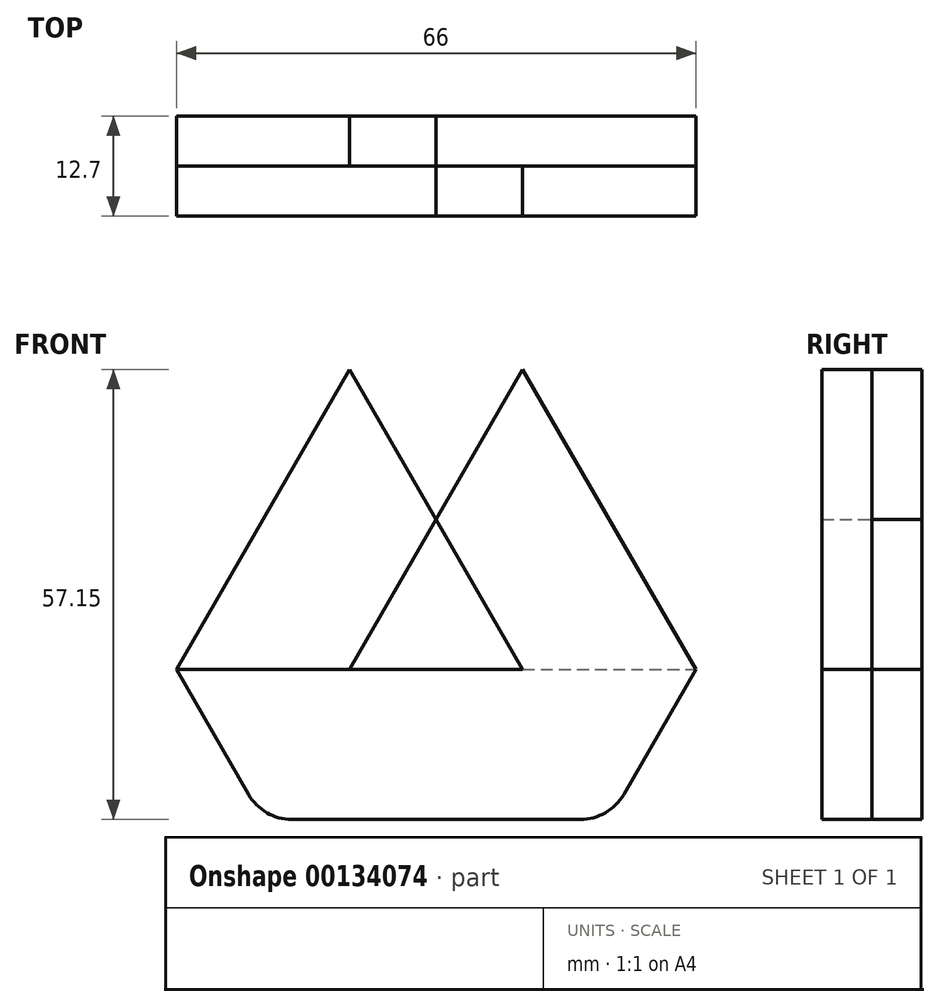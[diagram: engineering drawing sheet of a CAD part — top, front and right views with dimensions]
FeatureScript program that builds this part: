
annotation { "Feature Type Name" : "Feature", "Feature Type Description" : "" }
export const myFeature = defineFeature(function(context is Context, id is Id, definition is map)
    precondition{}
    {
        {
            var Q0;
            Q0=qCreatedBy(makeId("Front.planeOp"),FACE);
            var sketch = newSketch(context, id + "F0", { "sketchPlane" : qUnion([Q0])});
            skLineSegment(sketch, "E0", {"start": v(-11, 57.15) * mm, "end": v(0, 38.1) * mm});
            skLineSegment(sketch, "E1", {"start": v(0, 38.1) * mm, "end": v(11, 57.15) * mm});
            skLineSegment(sketch, "E2", {"start": v(0, 38.1) * mm, "end": v(-11, 19.05) * mm});
            skLineSegment(sketch, "E3", {"start": v(-11, 19.05) * mm, "end": v(11, 19.05) * mm});
            skLineSegment(sketch, "E4", {"start": v(11, 19.05) * mm, "end": v(0, 38.1) * mm});
            skLineSegment(sketch, "E5", {"start": v(11, 57.15) * mm, "end": v(33, 19.05) * mm});
            skLineSegment(sketch, "E6", {"start": v(33, 19.05) * mm, "end": v(23.83, 3.17) * mm});
            skLineSegment(sketch, "E7", {"start": v(18.33, 0) * mm, "end": v(-18.33, 0) * mm});
            skLineSegment(sketch, "E8", {"start": v(-23.83, 3.18) * mm, "end": v(-33, 19.05) * mm});
            skLineSegment(sketch, "E9", {"start": v(-33, 19.05) * mm, "end": v(-11, 57.15) * mm});
            skLineSegment(sketch, "E10", {"start": v(11, 19.05) * mm, "end": v(33, 19.05) * mm});
            skLineSegment(sketch, "E11", {"start": v(-11, 19.05) * mm, "end": v(-33, 19.05) * mm});
            skPoint(sketch, "E12", {"position": v(0, 25.4) * mm});
            skLineSegment(sketch, "E13", {"start": v(5.5, 28.58) * mm, "end": v(0, 25.4) * mm, "construction": true});
            skPoint(sketch, "E14.visualSharp", {"position": v(-22, 0) * mm});
            skArc(sketch, "E14.filletArc", {"start": v(-23.83, 3.18) * mm, "mid": v(-21.5, 0.85) * mm, "end": v(-18.33, 0) * mm});
            skPoint(sketch, "E15.visualSharp", {"position": v(22, 0) * mm});
            skArc(sketch, "E15.filletArc", {"start": v(18.33, 0) * mm, "mid": v(21.5, 0.85) * mm, "end": v(23.83, 3.18) * mm});
            skLineSegment(sketch, "E16", {"start": v(0, 38.1) * mm, "end": v(0, 19.05) * mm, "construction": true});
            skLineSegment(sketch, "E17", {"start": v(0, 19.05) * mm, "end": v(0, 0) * mm, "construction": true});
            skSolve(sketch);
        }
        {
            var Q0;
            Q0=makeQuery(id+"F0.imprint","IMPRINT",FACE,{"disambiguationData":[TD([[makeQuery(id+"F0.imprint","IMPRINT",EDGE,{"derivedFrom":sQuery(id+"F0.wireOp",EDGE,"E3")}),-1.0]])]});
            var Q1;
            Q1=makeQuery(id+"F0.imprint","IMPRINT",FACE,{"disambiguationData":[TD([[makeQuery(id+"F0.imprint","IMPRINT",EDGE,{"derivedFrom":sQuery(id+"F0.wireOp",EDGE,"E1")}),-1.0]])]});
            extrude(context, id + "F1", {"entities" : qUnion([Q0, Q1]), "depth" : 6.35 * mm});
        }
        {
            var Q0;
            Q0=makeQuery(id+"F0.imprint","IMPRINT",FACE,{"disambiguationData":[TD([[makeQuery(id+"F0.imprint","IMPRINT",EDGE,{"derivedFrom":sQuery(id+"F0.wireOp",EDGE,"E3")}),-1.0]])]});
            var Q1;
            Q1=makeQuery(id+"F0.imprint","IMPRINT",FACE,{"disambiguationData":[TD([[makeQuery(id+"F0.imprint","IMPRINT",EDGE,{"derivedFrom":sQuery(id+"F0.wireOp",EDGE,"E0")}),-1.0]])]});
            extrude(context, id + "F2", {"entities" : qUnion([Q0, Q1]), "oppositeDirection" : true, "depth" : 6.35 * mm});
        }
    });
